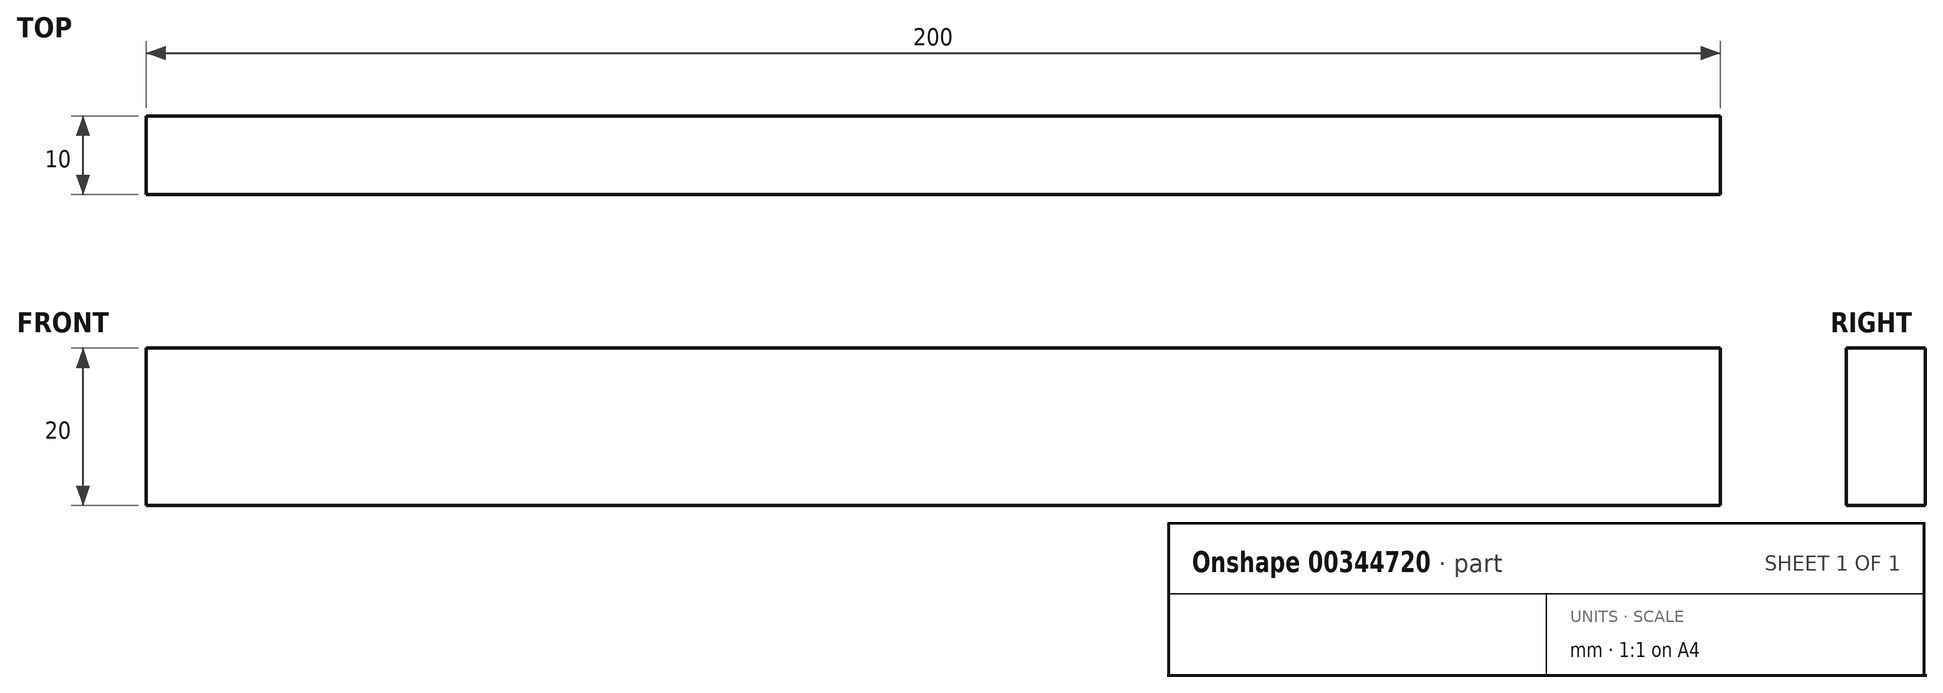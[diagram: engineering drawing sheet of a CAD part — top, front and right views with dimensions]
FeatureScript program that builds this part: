
annotation { "Feature Type Name" : "Feature", "Feature Type Description" : "" }
export const myFeature = defineFeature(function(context is Context, id is Id, definition is map)
    precondition{}
    {
        {
            var Q0;
            Q0=qCreatedBy(makeId("Top.planeOp"),FACE);
            var sketch = newSketch(context, id + "F0", { "sketchPlane" : qUnion([Q0])});
            skLineSegment(sketch, "E0.bottom", {"start": v(0, 0) * mm, "end": v(200, 0) * mm});
            skLineSegment(sketch, "E0.top", {"start": v(0, 10) * mm, "end": v(200, 10) * mm});
            skLineSegment(sketch, "E0.left", {"start": v(0, 0) * mm, "end": v(0, 10) * mm});
            skLineSegment(sketch, "E0.right", {"start": v(200, 0) * mm, "end": v(200, 10) * mm});
            skSolve(sketch);
        }
        {
            var Q0;
            Q0 = qSketchRegion(id + "F0", true);
            extrude(context, id + "F1", {"entities" : qUnion([Q0]), "depth" : 20 * mm});
        }
    });
